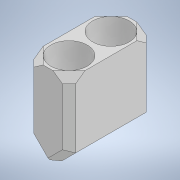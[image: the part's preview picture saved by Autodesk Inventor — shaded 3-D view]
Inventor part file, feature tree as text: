
AUTODESK INVENTOR PART (.ipt)
format: ipt  version: 2020 (Build 240168000, 168)  size: 183,296 bytes
history: native  units: mm
features: extrude x3, chamfer x3, sketch x3
ambient origin geometry x8: Origin, YZ Plane, XZ Plane, XY Plane, X Axis, Y Axis, Z Axis, Center Point
bodies: Solid1 (feature_tree)
feature tree (9):
  extrude  "Extrusion1"  Depth=5.5mm
  extrude  "Extrusion2"  Depth=3.166667mm
  extrude  "Extrusion3"  Depth=1.0mm
  chamfer  "Chamfer1"  Distance=3.15mm
  chamfer  "Chamfer2"  Distance=3.15mm
  chamfer  "Chamfer3"  Distance=10.0mm
  sketch  "Sketch1"  dims[d0=5.5mm d1=5.5mm]
  sketch  "Sketch2"  dims[d2=6.3mm d3=3.166667mm]
  sketch  "Sketch3"  dims[d4=3.15mm d5=3.15mm d6=3.15mm d7=3.15mm d8=10.0mm d9=0.0mm d11=45.0deg d12=45.0deg d13=12.6mm d14=0.0mm d15=2.0mm d16=2.0mm d17=2.0mm d18=2.0mm d19=2.54mm d20=2.54mm d21=1.27mm d22=1.27mm d23=4.0mm d24=0.0mm d25=1.5mm d26=2.0mm d27=45.0deg d28=1.0mm d29=2.0mm d30=45.0deg d31=1.0mm d32=2.0mm d33=45.0deg]
